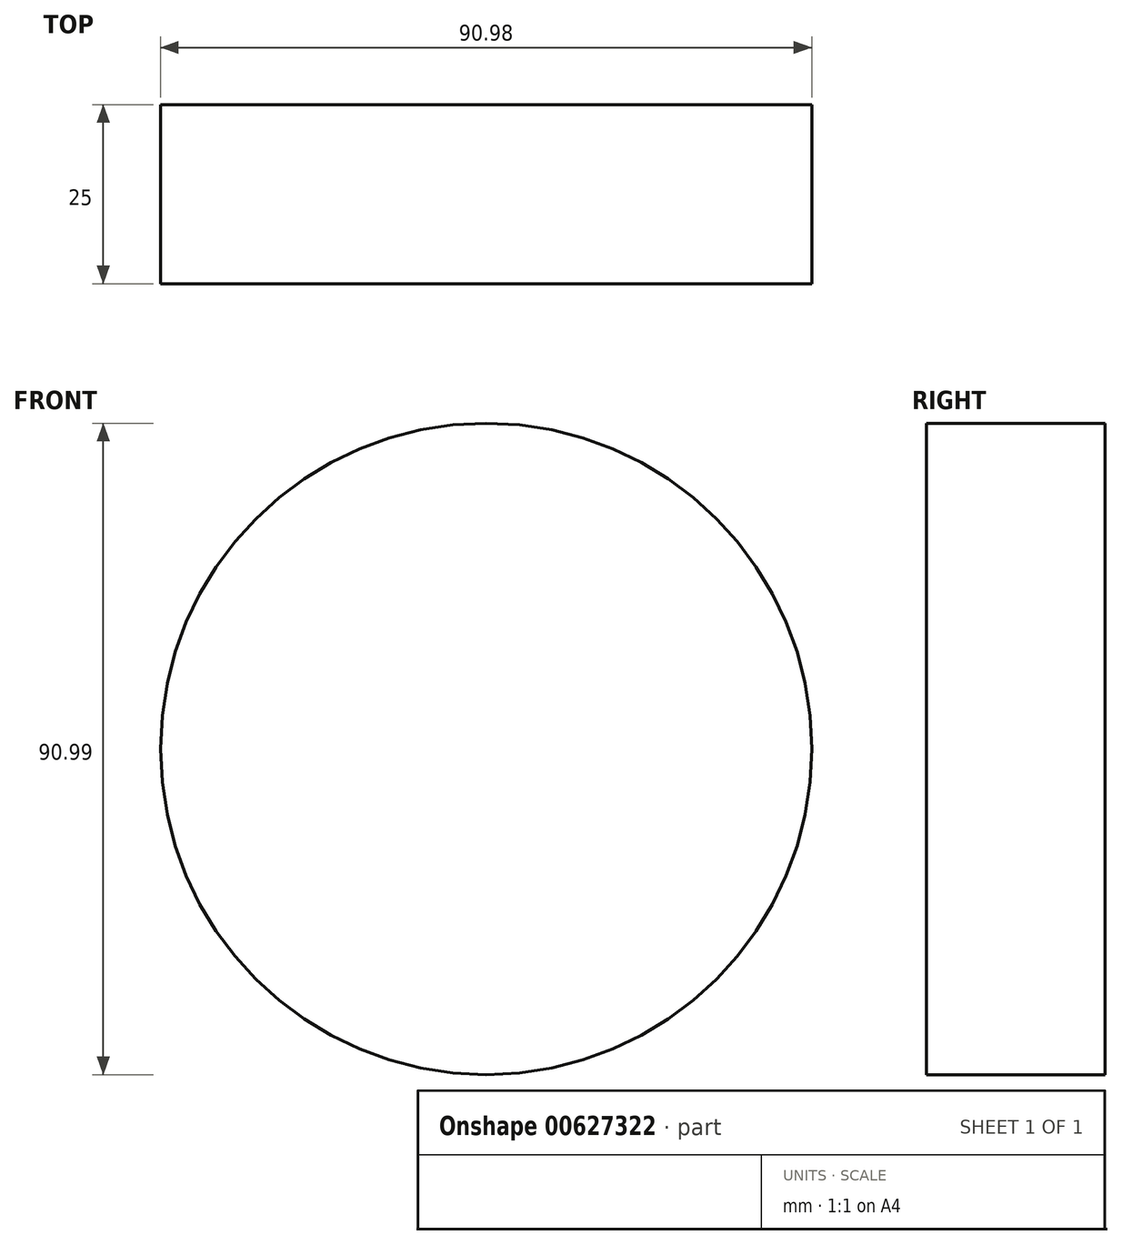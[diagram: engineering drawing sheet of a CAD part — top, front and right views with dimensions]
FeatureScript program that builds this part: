
annotation { "Feature Type Name" : "Feature", "Feature Type Description" : "" }
export const myFeature = defineFeature(function(context is Context, id is Id, definition is map)
    precondition{}
    {
        {
            var Q0;
            Q0=qCreatedBy(makeId("Front.planeOp"),FACE);
            var sketch = newSketch(context, id + "F0", { "sketchPlane" : qUnion([Q0])});
            skCircle(sketch, "E0", {"center": v(0, 26.4) * mm, "radius": 45.5 * mm});
            skSolve(sketch);
        }
        {
            var Q0;
            Q0=sQuery(id+"F0.wireOp",EDGE,"E0");
            extrude(context, id + "F1", {"bodyType" : ToolBodyType.SURFACE, "surfaceEntities" : qUnion([Q0]), "depth" : 25 * mm, "offsetDistance" : 25 * mm});
        }
    });
